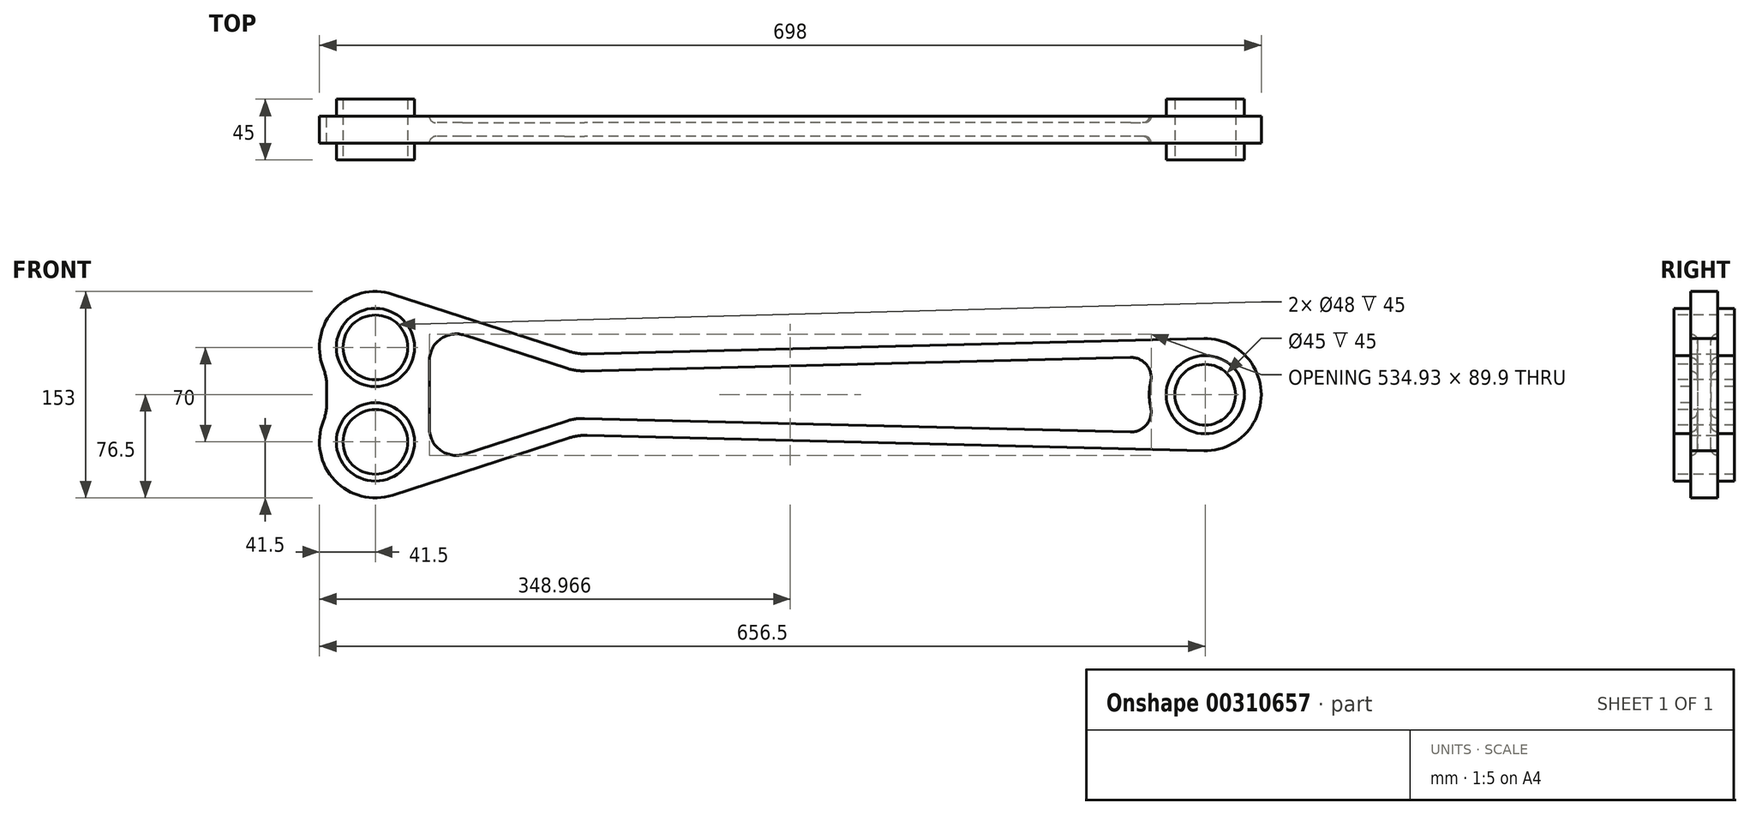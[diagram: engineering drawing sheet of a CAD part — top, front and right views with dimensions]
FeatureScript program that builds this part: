
annotation { "Feature Type Name" : "Feature", "Feature Type Description" : "" }
export const myFeature = defineFeature(function(context is Context, id is Id, definition is map)
    precondition{}
    {
        {
            var Q0;
            Q0=qCreatedBy(makeId("Front.planeOp"),FACE);
            var sketch = newSketch(context, id + "F0", { "sketchPlane" : qUnion([Q0])});
            skArc(sketch, "E0", {"start": v(33.9, 2.5) * mm, "mid": v(-34, 0) * mm, "end": v(33.9, -2.5) * mm, "construction": true});
            skCircle(sketch, "E1", {"center": v(700, 0) * mm, "radius": 29 * mm});
            skCircle(sketch, "E2", {"center": v(85, 35) * mm, "radius": 29 * mm});
            skCircle(sketch, "E3", {"center": v(85, -35) * mm, "radius": 29 * mm});
            skArc(sketch, "E4", {"start": v(97.8, 74.48) * mm, "mid": v(54.85, 63.51) * mm, "end": v(46.3, 20.01) * mm});
            skArc(sketch, "E5", {"start": v(46.3, -20.01) * mm, "mid": v(54.85, -63.51) * mm, "end": v(97.8, -74.48) * mm});
            skArc(sketch, "E6", {"start": v(698.97, -41.49) * mm, "mid": v(741.5, 0) * mm, "end": v(698.97, 41.49) * mm});
            skLineSegment(sketch, "E7", {"start": v(698.97, 41.49) * mm, "end": v(241.83, 30.17) * mm});
            skLineSegment(sketch, "E8", {"start": v(698.97, -41.49) * mm, "end": v(241.83, -30.17) * mm});
            skLineSegment(sketch, "E9", {"start": v(228.5, 32.1) * mm, "end": v(97.8, 74.48) * mm});
            skLineSegment(sketch, "E10", {"start": v(228.5, -32.1) * mm, "end": v(97.8, -74.48) * mm});
            skLineSegment(sketch, "E11", {"start": v(49, 5.57) * mm, "end": v(49, -5.57) * mm});
            skPoint(sketch, "E12.visualSharp", {"position": v(49, 14.35) * mm});
            skArc(sketch, "E12.filletArc", {"start": v(49, 5.57) * mm, "mid": v(48.32, 12.92) * mm, "end": v(46.3, 20.01) * mm});
            skPoint(sketch, "E13.visualSharp", {"position": v(49, -14.35) * mm});
            skArc(sketch, "E13.filletArc", {"start": v(46.3, -20.01) * mm, "mid": v(48.32, -12.92) * mm, "end": v(49, -5.57) * mm});
            skPoint(sketch, "E14.visualSharp", {"position": v(235, -30) * mm});
            skArc(sketch, "E14.filletArc", {"start": v(241.83, -30.17) * mm, "mid": v(235.08, -30.57) * mm, "end": v(228.5, -32.1) * mm});
            skPoint(sketch, "E15.visualSharp", {"position": v(235, 30) * mm});
            skArc(sketch, "E15.filletArc", {"start": v(228.5, 32.1) * mm, "mid": v(235.08, 30.57) * mm, "end": v(241.83, 30.17) * mm});
            skLineSegment(sketch, "E16", {"start": v(33.9, 2.5) * mm, "end": v(38.9, 2.5) * mm, "construction": true});
            skLineSegment(sketch, "E17", {"start": v(38.9, 2.5) * mm, "end": v(38.9, -2.5) * mm, "construction": true});
            skLineSegment(sketch, "E18", {"start": v(38.9, -2.5) * mm, "end": v(33.9, -2.5) * mm, "construction": true});
            skLineSegment(sketch, "E19", {"start": v(315, 31.98) * mm, "end": v(315, -31.98) * mm, "construction": true});
            skLineSegment(sketch, "E20", {"start": v(235, 30) * mm, "end": v(315, 30) * mm, "construction": true});
            skSolve(sketch);
        }
        {
            var Q0;
            Q0=qSketchRegion(id+"F0",true);
            extrude(context, id + "F1", {"entities" : qUnion([Q0]), "depth" : 20 * mm});
        }
        {
            var Q0;
            Q0=makeQuery(id+"F1.opExtrude","CAP_FACE",FACE,{"disambiguationData":[OSD([sQuery(id+"F0.wireOp",EDGE,"E1"),sQuery(id+"F0.wireOp",EDGE,"E2"),sQuery(id+"F0.wireOp",EDGE,"E3"),sQuery(id+"F0.wireOp",EDGE,"E4"),sQuery(id+"F0.wireOp",EDGE,"E5"),sQuery(id+"F0.wireOp",EDGE,"E6"),sQuery(id+"F0.wireOp",EDGE,"E7"),sQuery(id+"F0.wireOp",EDGE,"E8"),sQuery(id+"F0.wireOp",EDGE,"E9"),sQuery(id+"F0.wireOp",EDGE,"E10"),sQuery(id+"F0.wireOp",EDGE,"E11"),sQuery(id+"F0.wireOp",EDGE,"E12.filletArc"),sQuery(id+"F0.wireOp",EDGE,"E13.filletArc"),sQuery(id+"F0.wireOp",EDGE,"E14.filletArc"),sQuery(id+"F0.wireOp",EDGE,"E15.filletArc")])],"isStart":false});
            var sketch = newSketch(context, id + "F2", { "sketchPlane" : qUnion([Q0])});
            skArc(sketch, "E21", {"start": v(659.55, 9.28) * mm, "mid": v(658.5, 0) * mm, "end": v(659.55, -9.28) * mm});
            skLineSegment(sketch, "E22", {"start": v(644.56, 27.64) * mm, "end": v(240, 17.62) * mm});
            skLineSegment(sketch, "E23", {"start": v(226.68, 19.56) * mm, "end": v(151.17, 44.04) * mm});
            skLineSegment(sketch, "E24", {"start": v(125, 25.01) * mm, "end": v(125, -25.01) * mm});
            skLineSegment(sketch, "E25", {"start": v(151.17, -44.04) * mm, "end": v(226.68, -19.56) * mm});
            skLineSegment(sketch, "E26", {"start": v(240, -17.62) * mm, "end": v(644.56, -27.64) * mm});
            skPoint(sketch, "E27", {"position": v(85, -35) * mm});
            skPoint(sketch, "E28.visualSharp", {"position": v(669.6, 28.26) * mm});
            skArc(sketch, "E28.filletArc", {"start": v(659.55, 9.28) * mm, "mid": v(656.55, 22.13) * mm, "end": v(644.56, 27.64) * mm});
            skPoint(sketch, "E29.visualSharp", {"position": v(669.6, -28.26) * mm});
            skArc(sketch, "E29.filletArc", {"start": v(644.56, -27.64) * mm, "mid": v(656.55, -22.13) * mm, "end": v(659.55, -9.28) * mm});
            skPoint(sketch, "E30.visualSharp", {"position": v(125, 52.52) * mm});
            skArc(sketch, "E30.filletArc", {"start": v(151.17, 44.04) * mm, "mid": v(133.24, 41.19) * mm, "end": v(125, 25.01) * mm});
            skPoint(sketch, "E31.visualSharp", {"position": v(125, -52.52) * mm});
            skArc(sketch, "E31.filletArc", {"start": v(125, -25.01) * mm, "mid": v(133.24, -41.19) * mm, "end": v(151.17, -44.04) * mm});
            skPoint(sketch, "E32.visualSharp", {"position": v(233.18, 17.45) * mm});
            skArc(sketch, "E32.filletArc", {"start": v(226.68, 19.56) * mm, "mid": v(233.26, 18.02) * mm, "end": v(240, 17.62) * mm});
            skPoint(sketch, "E33.visualSharp", {"position": v(233.18, -17.45) * mm});
            skArc(sketch, "E33.filletArc", {"start": v(240, -17.62) * mm, "mid": v(233.26, -18.02) * mm, "end": v(226.68, -19.56) * mm});
            skSolve(sketch);
        }
        {
            var Q0;
            Q0=qSketchRegion(id+"F2",true);
            extrude(context, id + "F3", {"entities" : qUnion([Q0]), "operationType" : NewBodyOperationType.REMOVE, "oppositeDirection" : true, "depth" : 5 * mm});
        }
        {
            var Q0;
            Q0=makeQuery(id+"F1.opExtrude","CAP_FACE",FACE,{"disambiguationData":[OSD([sQuery(id+"F0.wireOp",EDGE,"E1"),sQuery(id+"F0.wireOp",EDGE,"E2"),sQuery(id+"F0.wireOp",EDGE,"E3"),sQuery(id+"F0.wireOp",EDGE,"E4"),sQuery(id+"F0.wireOp",EDGE,"E5"),sQuery(id+"F0.wireOp",EDGE,"E6"),sQuery(id+"F0.wireOp",EDGE,"E7"),sQuery(id+"F0.wireOp",EDGE,"E8"),sQuery(id+"F0.wireOp",EDGE,"E9"),sQuery(id+"F0.wireOp",EDGE,"E10"),sQuery(id+"F0.wireOp",EDGE,"E11"),sQuery(id+"F0.wireOp",EDGE,"E12.filletArc"),sQuery(id+"F0.wireOp",EDGE,"E13.filletArc"),sQuery(id+"F0.wireOp",EDGE,"E14.filletArc"),sQuery(id+"F0.wireOp",EDGE,"E15.filletArc")])],"isStart":true});
            var sketch = newSketch(context, id + "F4", { "sketchPlane" : qUnion([Q0])});
            skArc(sketch, "E34", {"start": v(-659.55, -9.28) * mm, "mid": v(-658.5, 0) * mm, "end": v(-659.55, 9.28) * mm});
            skLineSegment(sketch, "E35", {"start": v(-644.56, 27.64) * mm, "end": v(-240, 17.62) * mm});
            skLineSegment(sketch, "E36", {"start": v(-226.68, 19.56) * mm, "end": v(-151.17, 44.04) * mm});
            skLineSegment(sketch, "E37", {"start": v(-125, 25.01) * mm, "end": v(-125, -25.01) * mm});
            skLineSegment(sketch, "E38", {"start": v(-151.17, -44.04) * mm, "end": v(-226.68, -19.56) * mm});
            skLineSegment(sketch, "E39", {"start": v(-240, -17.62) * mm, "end": v(-644.56, -27.64) * mm});
            skPoint(sketch, "E40", {"position": v(-85, 35) * mm});
            skPoint(sketch, "E41.visualSharp", {"position": v(-669.6, 28.26) * mm});
            skArc(sketch, "E41.filletArc", {"start": v(-644.56, 27.64) * mm, "mid": v(-656.55, 22.13) * mm, "end": v(-659.55, 9.28) * mm});
            skPoint(sketch, "E42.visualSharp", {"position": v(-669.6, -28.26) * mm});
            skArc(sketch, "E42.filletArc", {"start": v(-659.55, -9.28) * mm, "mid": v(-656.55, -22.13) * mm, "end": v(-644.56, -27.64) * mm});
            skPoint(sketch, "E43.visualSharp", {"position": v(-125, 52.52) * mm});
            skArc(sketch, "E43.filletArc", {"start": v(-125, 25.01) * mm, "mid": v(-133.24, 41.19) * mm, "end": v(-151.17, 44.04) * mm});
            skPoint(sketch, "E44.visualSharp", {"position": v(-125, -52.52) * mm});
            skArc(sketch, "E44.filletArc", {"start": v(-151.17, -44.04) * mm, "mid": v(-133.24, -41.19) * mm, "end": v(-125, -25.01) * mm});
            skPoint(sketch, "E45.visualSharp", {"position": v(-233.18, -17.45) * mm});
            skArc(sketch, "E45.filletArc", {"start": v(-226.68, -19.56) * mm, "mid": v(-233.26, -18.02) * mm, "end": v(-240, -17.62) * mm});
            skPoint(sketch, "E46.visualSharp", {"position": v(-233.18, 17.45) * mm});
            skArc(sketch, "E46.filletArc", {"start": v(-240, 17.62) * mm, "mid": v(-233.26, 18.02) * mm, "end": v(-226.68, 19.56) * mm});
            skSolve(sketch);
        }
        {
            var Q0;
            Q0=qSketchRegion(id+"F4",true);
            extrude(context, id + "F5", {"entities" : qUnion([Q0]), "operationType" : NewBodyOperationType.REMOVE, "oppositeDirection" : true, "depth" : 5 * mm});
        }
        {
            var Q0;
            Q0=makeQuery(id+"F3.boolean.opBoolean","COPY",EDGE,{"derivedFrom":makeQuery(id+"F3.opExtrude","CAP_EDGE",EDGE,{"disambiguationData":[OSD([sQuery(id+"F2.wireOp",EDGE,"E22")])],"isStart":false})});
            fillet(context, id + "F6", {"entities" : qUnion([Q0]), "radius" : 5 * mm, "tangentPropagation" : true, "allowEdgeOverflow" : false});
        }
        {
            var Q0;
            Q0=makeQuery(id+"F5.boolean.opBoolean","COPY",EDGE,{"derivedFrom":makeQuery(id+"F5.opExtrude","CAP_EDGE",EDGE,{"disambiguationData":[OSD([sQuery(id+"F4.wireOp",EDGE,"E35")])],"isStart":false})});
            fillet(context, id + "F7", {"entities" : qUnion([Q0]), "radius" : 5 * mm, "tangentPropagation" : true, "allowEdgeOverflow" : false});
        }
        {
            var Q0;
            Q0=makeQuery(id+"F1.opExtrude","CAP_FACE",FACE,{"disambiguationData":[OSD([sQuery(id+"F0.wireOp",EDGE,"E1"),sQuery(id+"F0.wireOp",EDGE,"E2"),sQuery(id+"F0.wireOp",EDGE,"E3"),sQuery(id+"F0.wireOp",EDGE,"E4"),sQuery(id+"F0.wireOp",EDGE,"E5"),sQuery(id+"F0.wireOp",EDGE,"E6"),sQuery(id+"F0.wireOp",EDGE,"E7"),sQuery(id+"F0.wireOp",EDGE,"E8"),sQuery(id+"F0.wireOp",EDGE,"E9"),sQuery(id+"F0.wireOp",EDGE,"E10"),sQuery(id+"F0.wireOp",EDGE,"E11"),sQuery(id+"F0.wireOp",EDGE,"E12.filletArc"),sQuery(id+"F0.wireOp",EDGE,"E13.filletArc"),sQuery(id+"F0.wireOp",EDGE,"E14.filletArc"),sQuery(id+"F0.wireOp",EDGE,"E15.filletArc")])],"isStart":true});
            var sketch = newSketch(context, id + "F8", { "sketchPlane" : qUnion([Q0])});
            skCircle(sketch, "E47", {"center": v(-700, 0) * mm, "radius": 22.5 * mm});
            skCircle(sketch, "E48", {"center": v(-700, 0) * mm, "radius": 29 * mm});
            skCircle(sketch, "E49", {"center": v(-85, 35) * mm, "radius": 29 * mm});
            skCircle(sketch, "E50", {"center": v(-85, 35) * mm, "radius": 24 * mm});
            skCircle(sketch, "E51", {"center": v(-85, -35) * mm, "radius": 29 * mm});
            skCircle(sketch, "E52", {"center": v(-85, -35) * mm, "radius": 24 * mm});
            skSolve(sketch);
        }
        {
            var Q0;
            Q0=qSketchRegion(id+"F8",true);
            extrude(context, id + "F9", {"entities" : qUnion([Q0]), "operationType" : NewBodyOperationType.ADD, "depth" : 12.5 * mm, "hasSecondDirection" : true, "secondDirectionOppositeDirection" : true, "secondDirectionDepth" : 32.5 * mm});
        }
    });
